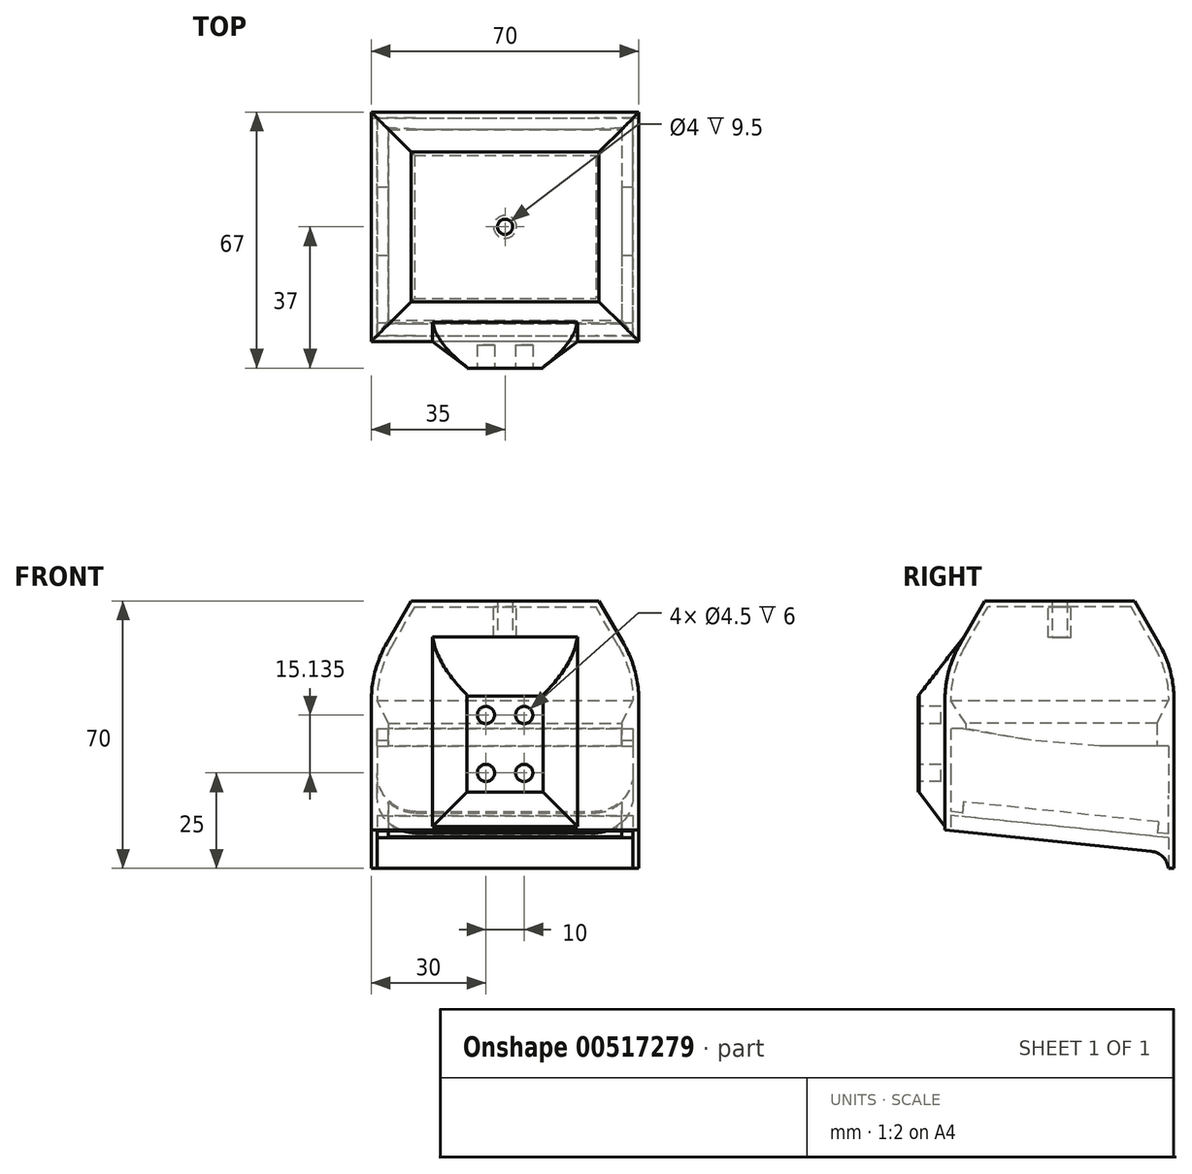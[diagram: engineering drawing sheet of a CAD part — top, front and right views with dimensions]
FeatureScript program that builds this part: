
annotation { "Feature Type Name" : "Feature", "Feature Type Description" : "" }
export const myFeature = defineFeature(function(context is Context, id is Id, definition is map)
    precondition{}
    {
        {
            var Q0;
            Q0=qCreatedBy(makeId("Top.planeOp"),FACE);
            var sketch = newSketch(context, id + "F0", { "sketchPlane" : qUnion([Q0])});
            skLineSegment(sketch, "E0.bottom", {"start": v(-35, 30) * mm, "end": v(35, 30) * mm});
            skLineSegment(sketch, "E0.top", {"start": v(-35, -30) * mm, "end": v(35, -30) * mm});
            skLineSegment(sketch, "E0.left", {"start": v(-35, 30) * mm, "end": v(-35, -30) * mm});
            skLineSegment(sketch, "E0.right", {"start": v(35, 30) * mm, "end": v(35, -30) * mm});
            skSolve(sketch);
        }
        {
            var Q0;
            Q0 = qSketchRegion(id + "F0", true);
            extrude(context, id + "F1", {"entities" : qUnion([Q0]), "endBound" : BoundingType.SYMMETRIC, "depth" : 70 * mm, "offsetDistance" : 25 * mm});
        }
        {
            var Q0;
            Q0=makeQuery(id+"F1.opExtrude","CAP_FACE",FACE,{"disambiguationData":[OSD([sQuery(id+"F0.wireOp",EDGE,"E0.bottom"),sQuery(id+"F0.wireOp",EDGE,"E0.top"),sQuery(id+"F0.wireOp",EDGE,"E0.left"),sQuery(id+"F0.wireOp",EDGE,"E0.right")])],"isStart":false});
            chamfer(context, id + "F2", {"entities" : qUnion([Q0]), "chamferType" : ChamferType.OFFSET_ANGLE, "width" : 18 * mm, "oppositeDirection" : false, "angle" : 30 * degree, "tangentPropagation" : true});
        }
        {
            var Q0;
            {var subQ0=sQuery(id+"F0.wireOp",EDGE,"E0.bottom");Q0=makeQuery(id+"F2.opChamfer","BLEND_EDGE",EDGE,{"blendedFrom":[makeQuery(id+"F1.opExtrude","CAP_EDGE",EDGE,{"disambiguationData":[OSD([subQ0])],"isStart":false}),makeQuery(id+"F1.opExtrude","SWEPT_FACE",FACE,{"disambiguationData":[OSD([subQ0])]})],"blendedInto":[makeQuery(id+"F1.opExtrude","SWEPT_FACE",FACE,{"disambiguationData":[OSD([subQ0])]})]});}
            var Q1;
            {var subQ0=sQuery(id+"F0.wireOp",EDGE,"E0.left");Q1=makeQuery(id+"F2.opChamfer","BLEND_EDGE",EDGE,{"blendedFrom":[makeQuery(id+"F1.opExtrude","CAP_EDGE",EDGE,{"disambiguationData":[OSD([subQ0])],"isStart":false}),makeQuery(id+"F1.opExtrude","SWEPT_FACE",FACE,{"disambiguationData":[OSD([subQ0])]})],"blendedInto":[makeQuery(id+"F1.opExtrude","SWEPT_FACE",FACE,{"disambiguationData":[OSD([subQ0])]})]});}
            var Q2;
            {var subQ0=sQuery(id+"F0.wireOp",EDGE,"E0.right");Q2=makeQuery(id+"F2.opChamfer","BLEND_EDGE",EDGE,{"blendedFrom":[makeQuery(id+"F1.opExtrude","CAP_EDGE",EDGE,{"disambiguationData":[OSD([subQ0])],"isStart":false}),makeQuery(id+"F1.opExtrude","SWEPT_FACE",FACE,{"disambiguationData":[OSD([subQ0])]})],"blendedInto":[makeQuery(id+"F1.opExtrude","SWEPT_FACE",FACE,{"disambiguationData":[OSD([subQ0])]})]});}
            var Q3;
            {var subQ0=sQuery(id+"F0.wireOp",EDGE,"E0.top");Q3=makeQuery(id+"F2.opChamfer","BLEND_EDGE",EDGE,{"blendedFrom":[makeQuery(id+"F1.opExtrude","CAP_EDGE",EDGE,{"disambiguationData":[OSD([subQ0])],"isStart":false}),makeQuery(id+"F1.opExtrude","SWEPT_FACE",FACE,{"disambiguationData":[OSD([subQ0])]})],"blendedInto":[makeQuery(id+"F1.opExtrude","SWEPT_FACE",FACE,{"disambiguationData":[OSD([subQ0])]})]});}
            fillet(context, id + "F3", {"entities" : qUnion([Q0, Q1, Q2, Q3]), "radius" : 30 * mm, "tangentPropagation" : true, "allowEdgeOverflow" : false});
        }
        {
            var Q0;
            Q0=makeQuery(id+"F1.opExtrude","CAP_FACE",FACE,{"disambiguationData":[OSD([sQuery(id+"F0.wireOp",EDGE,"E0.bottom"),sQuery(id+"F0.wireOp",EDGE,"E0.top"),sQuery(id+"F0.wireOp",EDGE,"E0.left"),sQuery(id+"F0.wireOp",EDGE,"E0.right")])],"isStart":true});
            var Q1;
            Q1=makeQuery(id+"F1.opExtrude","SWEPT_BODY",BODY,{"disambiguationData":[OSD([sQuery(id+"F0.wireOp",EDGE,"E0.bottom"),sQuery(id+"F0.wireOp",EDGE,"E0.top"),sQuery(id+"F0.wireOp",EDGE,"E0.left"),sQuery(id+"F0.wireOp",EDGE,"E0.right")])]});
            shell(context, id + "F4", {"entities" : qUnion([Q0]), "parts" : qUnion([Q1]), "thickness" : 1.5 * mm});
        }
        {
            var Q0;
            Q0=makeQuery(id+"F1.opExtrude","SWEPT_FACE",FACE,{"disambiguationData":[OSD([sQuery(id+"F0.wireOp",EDGE,"E0.top")])]});
            var sketch = newSketch(context, id + "F5", { "sketchPlane" : qUnion([Q0])});
            skLineSegment(sketch, "E1.bottom", {"start": v(-10, 10) * mm, "end": v(10, 10) * mm});
            skLineSegment(sketch, "E1.top", {"start": v(-10, -15) * mm, "end": v(10, -15) * mm});
            skLineSegment(sketch, "E1.left", {"start": v(-10, 10) * mm, "end": v(-10, -15) * mm});
            skLineSegment(sketch, "E1.right", {"start": v(10, 10) * mm, "end": v(10, -15) * mm});
            skSolve(sketch);
        }
        {
            var Q0;
            Q0 = qSketchRegion(id + "F5", true);
            extrude(context, id + "F6", {"entities" : qUnion([Q0]), "operationType" : NewBodyOperationType.ADD, "depth" : 7 * mm, "offsetDistance" : 25 * mm, "hasSecondDirection" : true, "secondDirectionOppositeDirection" : true, "secondDirectionDepth" : 1.5 * mm});
        }
        {
            var Q0;
            Q0=makeQuery(id+"F6.boolean.opBoolean","INTERSECT",EDGE,{"derivedFrom":[makeQuery(id+"F3.opFillet","BLEND_FACE",FACE,{"disambiguationData":[OSD([sQuery(id+"F0.wireOp",EDGE,"E0.top")])]}),makeQuery(id+"F6.opExtrude","SWEPT_FACE",FACE,{"disambiguationData":[OSD([sQuery(id+"F5.wireOp",EDGE,"E1.bottom")])]})]});
            chamfer(context, id + "F7", {"entities" : qUnion([Q0]), "chamferType" : ChamferType.OFFSET_ANGLE, "width" : 15 * mm, "oppositeDirection" : false, "angle" : 58 * degree, "tangentPropagation" : true});
        }
        {
            var Q0;
            Q0=makeQuery(id+"F6.boolean.opBoolean","INTERSECT",EDGE,{"derivedFrom":[makeQuery(id+"F1.opExtrude","SWEPT_FACE",FACE,{"disambiguationData":[OSD([sQuery(id+"F0.wireOp",EDGE,"E0.top")])]}),makeQuery(id+"F6.opExtrude","SWEPT_FACE",FACE,{"disambiguationData":[OSD([sQuery(id+"F5.wireOp",EDGE,"E1.right")])]})]});
            var Q1;
            Q1=makeQuery(id+"F6.boolean.opBoolean","INTERSECT",EDGE,{"derivedFrom":[makeQuery(id+"F1.opExtrude","SWEPT_FACE",FACE,{"disambiguationData":[OSD([sQuery(id+"F0.wireOp",EDGE,"E0.top")])]}),makeQuery(id+"F6.opExtrude","SWEPT_FACE",FACE,{"disambiguationData":[OSD([sQuery(id+"F5.wireOp",EDGE,"E1.top")])]})]});
            var Q2;
            Q2=makeQuery(id+"F6.boolean.opBoolean","INTERSECT",EDGE,{"derivedFrom":[makeQuery(id+"F1.opExtrude","SWEPT_FACE",FACE,{"disambiguationData":[OSD([sQuery(id+"F0.wireOp",EDGE,"E0.top")])]}),makeQuery(id+"F6.opExtrude","SWEPT_FACE",FACE,{"disambiguationData":[OSD([sQuery(id+"F5.wireOp",EDGE,"E1.left")])]})]});
            chamfer(context, id + "F8", {"entities" : qUnion([Q0, Q1, Q2]), "chamferType" : ChamferType.OFFSET_ANGLE, "width" : 9 * mm, "oppositeDirection" : false, "angle" : 37 * degree, "tangentPropagation" : true});
        }
        {
            var Q0;
            Q0=makeQuery(id+"F6.opExtrude","CAP_FACE",FACE,{"disambiguationData":[OSD([sQuery(id+"F5.wireOp",EDGE,"E1.bottom"),sQuery(id+"F5.wireOp",EDGE,"E1.top"),sQuery(id+"F5.wireOp",EDGE,"E1.left"),sQuery(id+"F5.wireOp",EDGE,"E1.right")])],"isStart":false});
            var sketch = newSketch(context, id + "F9", { "sketchPlane" : qUnion([Q0])});
            skLineSegment(sketch, "E2.0", {"start": v(5, -10) * mm, "end": v(5, 5.14) * mm, "construction": true});
            skLineSegment(sketch, "E2.1", {"start": v(-5, -10) * mm, "end": v(5, -10) * mm, "construction": true});
            skLineSegment(sketch, "E2.2", {"start": v(-5, 5.14) * mm, "end": v(-5, -10) * mm, "construction": true});
            skLineSegment(sketch, "E2.3", {"start": v(5, 5.14) * mm, "end": v(-5, 5.14) * mm, "construction": true});
            skCircle(sketch, "E3", {"center": v(-5, 5.14) * mm, "radius": 2.25 * mm});
            skCircle(sketch, "E4.MirrorC", {"center": v(5, 5.14) * mm, "radius": 2.25 * mm});
            skCircle(sketch, "E5", {"center": v(-5, -10) * mm, "radius": 2.25 * mm});
            skCircle(sketch, "E6.MirrorC", {"center": v(5, -10) * mm, "radius": 2.25 * mm});
            skSolve(sketch);
        }
        {
            var Q0;
            Q0 = qSketchRegion(id + "F9", true);
            extrude(context, id + "F10", {"entities" : qUnion([Q0]), "operationType" : NewBodyOperationType.REMOVE, "oppositeDirection" : true, "depth" : 6 * mm, "offsetDistance" : 25 * mm});
        }
        {
            var Q0;
            Q0=makeQuery(id+"F1.opExtrude","SWEPT_FACE",FACE,{"disambiguationData":[OSD([sQuery(id+"F0.wireOp",EDGE,"E0.left")])]});
            var sketch = newSketch(context, id + "F11", { "sketchPlane" : qUnion([Q0])});
            skLineSegment(sketch, "E7", {"start": v(-28.5, -35) * mm, "end": v(30, -35) * mm});
            skLineSegment(sketch, "E8", {"start": v(30, -35) * mm, "end": v(30, -25) * mm});
            skLineSegment(sketch, "E9", {"start": v(30, -25) * mm, "end": v(-28.5, -31) * mm});
            skLineSegment(sketch, "E10", {"start": v(-28.5, -31) * mm, "end": v(-28.5, -35) * mm});
            skSolve(sketch);
        }
        {
            var Q0;
            Q0 = qSketchRegion(id + "F11", true);
            extrude(context, id + "F12", {"entities" : qUnion([Q0]), "operationType" : NewBodyOperationType.REMOVE, "endBound" : BoundingType.THROUGH_ALL, "oppositeDirection" : true, "depth" : 25 * mm, "offsetDistance" : 25 * mm});
        }
        {
            var Q0;
            {var subQ0=sQuery(id+"F11.wireOp",EDGE,"E9");var subQ2=sQuery(id+"F0.wireOp",EDGE,"E0.left");var subQ3=makeQuery(id+"F1.opExtrude","SWEPT_FACE",FACE,{"disambiguationData":[OSD([subQ2])]});var subQ4=sQuery(id+"F11.wireOp",EDGE,"E10");Q0=makeQuery(id+"F12.boolean.opBoolean","COPY",EDGE,{"disambiguationData":[TD([subQ3])],"derivedFrom":makeQuery(id+"F12.opExtrude","SWEPT_EDGE",EDGE,{"disambiguationData":[OSD([subQ0,subQ4])]})});}
            var Q1;
            {var subQ1=sQuery(id+"F11.wireOp",EDGE,"E9");var subQ2=sQuery(id+"F0.wireOp",EDGE,"E0.right");var subQ3=makeQuery(id+"F1.opExtrude","SWEPT_FACE",FACE,{"disambiguationData":[OSD([subQ2])]});var subQ4=sQuery(id+"F11.wireOp",EDGE,"E10");Q1=makeQuery(id+"F12.boolean.opBoolean","COPY",EDGE,{"disambiguationData":[TD([subQ3])],"derivedFrom":makeQuery(id+"F12.opExtrude","SWEPT_EDGE",EDGE,{"disambiguationData":[OSD([subQ1,subQ4])]})});}
            fillet(context, id + "F13", {"entities" : qUnion([Q0, Q1]), "radius" : 5 * mm, "tangentPropagation" : true, "allowEdgeOverflow" : false});
        }
        {
            var Q0;
            {var subQ0=sQuery(id+"F0.wireOp",EDGE,"E0.top");Q0=makeQuery(id+"F4.opShell","OFFSET_FACE",FACE,{"disambiguationData":[OSD([subQ0]),TDD([makeQuery(id+"F1.opExtrude","SWEPT_FACE",FACE,{"disambiguationData":[OSD([subQ0])]})])]});}
            var sketch = newSketch(context, id + "F14", { "sketchPlane" : qUnion([Q0])});
            skLineSegment(sketch, "E11", {"start": v(-33.5, 8.96) * mm, "end": v(-33.5, 2.96) * mm});
            skLineSegment(sketch, "E12", {"start": v(-33.5, 2.96) * mm, "end": v(-30.5, 2.96) * mm});
            skLineSegment(sketch, "E13", {"start": v(-30.5, 2.96) * mm, "end": v(-33.5, 8.96) * mm});
            skLineSegment(sketch, "E14", {"start": v(33.5, 8.96) * mm, "end": v(33.5, 2.96) * mm});
            skLineSegment(sketch, "E15", {"start": v(33.5, 2.96) * mm, "end": v(30.5, 2.96) * mm});
            skLineSegment(sketch, "E16", {"start": v(30.5, 2.96) * mm, "end": v(33.5, 8.96) * mm});
            skSolve(sketch);
        }
        {
            var Q0;
            Q0 = qSketchRegion(id + "F14", true);
            extrude(context, id + "F15", {"entities" : qUnion([Q0]), "operationType" : NewBodyOperationType.ADD, "endBound" : BoundingType.UP_TO_NEXT, "depth" : 0 * mm, "offsetDistance" : 25 * mm});
        }
        {
            var Q0;
            {var subQ1=sQuery(id+"F0.wireOp",EDGE,"E0.right");Q0=makeQuery(id+"F18.boolean.opBoolean","SPLIT",FACE,{"disambiguationData":[TD([makeQuery(id+"F18.opExtrude","SWEPT_FACE",FACE,{"disambiguationData":[OSD([sQuery(id+"F17.wireOp",EDGE,"E25")])]})])],"derivedFrom":makeQuery(id+"F4.opShell","OFFSET_FACE",FACE,{"disambiguationData":[OSD([subQ1]),TDD([makeQuery(id+"F1.opExtrude","SWEPT_FACE",FACE,{"disambiguationData":[OSD([subQ1])]})])]})});}
            var sketch = newSketch(context, id + "F16", { "sketchPlane" : qUnion([Q0])});
            skLineSegment(sketch, "E17", {"start": v(28.5, 8.96) * mm, "end": v(28.5, 2.96) * mm});
            skLineSegment(sketch, "E18", {"start": v(28.5, 2.96) * mm, "end": v(24.5, 2.96) * mm});
            skLineSegment(sketch, "E19", {"start": v(24.5, 2.96) * mm, "end": v(28.5, 8.96) * mm});
            skLineSegment(sketch, "E20", {"start": v(-28.5, 8.96) * mm, "end": v(-28.5, 2.96) * mm});
            skLineSegment(sketch, "E21", {"start": v(-28.5, 2.96) * mm, "end": v(-25.5, 2.96) * mm});
            skLineSegment(sketch, "E22", {"start": v(-25.5, 2.96) * mm, "end": v(-28.5, 8.96) * mm});
            skSolve(sketch);
        }
        {
            var Q0;
            {var subQ0=sQuery(id+"F0.wireOp",EDGE,"E0.right");Q0=makeQuery(id+"F4.opShell","OFFSET_FACE",FACE,{"disambiguationData":[OSD([subQ0]),TDD([makeQuery(id+"F1.opExtrude","SWEPT_FACE",FACE,{"disambiguationData":[OSD([subQ0])]})])]});}
            var sketch = newSketch(context, id + "F17", { "sketchPlane" : qUnion([Q0])});
            skLineSegment(sketch, "E23", {"start": v(-28.5, -26.98) * mm, "end": v(28.5, -21.13) * mm});
            skLineSegment(sketch, "E24", {"start": v(28.5, -21.13) * mm, "end": v(28.5, -20.13) * mm});
            skLineSegment(sketch, "E25", {"start": v(28.5, -20.13) * mm, "end": v(-28.5, -25.98) * mm});
            skLineSegment(sketch, "E26", {"start": v(-28.5, -25.98) * mm, "end": v(-28.5, -26.98) * mm});
            skSolve(sketch);
        }
        {
            var Q0;
            Q0 = qSketchRegion(id + "F17", true);
            extrude(context, id + "F18", {"entities" : qUnion([Q0]), "operationType" : NewBodyOperationType.ADD, "endBound" : BoundingType.UP_TO_NEXT, "depth" : 25 * mm, "offsetDistance" : 25 * mm});
        }
        {
            var Q0;
            Q0=makeQuery(id+"F18.opExtrude","SWEPT_FACE",FACE,{"disambiguationData":[OSD([sQuery(id+"F17.wireOp",EDGE,"E23")])]});
            var sketch = newSketch(context, id + "F19", { "sketchPlane" : qUnion([Q0])});
            skLineSegment(sketch, "E27.0", {"start": v(30.5, 23.2) * mm, "end": v(-30.5, 23.2) * mm});
            skLineSegment(sketch, "E27.1", {"start": v(30.5, -28.1) * mm, "end": v(30.5, 23.2) * mm});
            skLineSegment(sketch, "E27.2", {"start": v(-30.5, -28.1) * mm, "end": v(30.5, -28.1) * mm});
            skLineSegment(sketch, "E27.3", {"start": v(-30.5, 23.2) * mm, "end": v(-30.5, -28.1) * mm});
            skSolve(sketch);
        }
        {
            var Q0;
            Q0 = qSketchRegion(id + "F19", true);
            extrude(context, id + "F20", {"entities" : qUnion([Q0]), "operationType" : NewBodyOperationType.REMOVE, "oppositeDirection" : true, "depth" : 1 * mm, "offsetDistance" : 25 * mm});
        }
        {
            var Q0;
            Q0=makeQuery(id+"F18.opExtrude","SWEPT_EDGE",EDGE,{"disambiguationData":[OSD([sQuery(id+"F0.wireOp",EDGE,"E0.top"),sQuery(id+"F0.wireOp",EDGE,"E0.right"),sQuery(id+"F17.wireOp",EDGE,"E24"),sQuery(id+"F17.wireOp",EDGE,"E25")])]});
            var Q1;
            Q1=makeQuery(id+"F18.opExtrude","CAP_EDGE",EDGE,{"disambiguationData":[OSD([sQuery(id+"F17.wireOp",EDGE,"E25")])],"isStart":true});
            var Q2;
            Q2=makeQuery(id+"F18.opExtrude","SWEPT_EDGE",EDGE,{"disambiguationData":[OSD([sQuery(id+"F0.wireOp",EDGE,"E0.bottom"),sQuery(id+"F0.wireOp",EDGE,"E0.right"),sQuery(id+"F17.wireOp",EDGE,"E25"),sQuery(id+"F17.wireOp",EDGE,"E26")])]});
            var Q3;
            Q3=makeQuery(id+"F18.opExtrude","CAP_EDGE",EDGE,{"disambiguationData":[OSD([sQuery(id+"F17.wireOp",EDGE,"E25")])],"isStart":false});
            fillet(context, id + "F21", {"entities" : qUnion([Q0, Q1, Q2, Q3]), "radius" : 10 * mm, "tangentPropagation" : true, "allowEdgeOverflow" : false});
        }
        {
            var Q0;
            Q0 = qSketchRegion(id + "F16", true);
            extrude(context, id + "F22", {"entities" : qUnion([Q0]), "operationType" : NewBodyOperationType.ADD, "depth" : 68 * mm, "offsetDistance" : 25 * mm});
        }
        {
            var Q0;
            {var subQ2=sQuery(id+"F0.wireOp",EDGE,"E0.right");Q0=makeQuery(id+"F18.boolean.opBoolean","SPLIT",FACE,{"disambiguationData":[TD([makeQuery(id+"F15.opExtrude","SWEPT_FACE",FACE,{"disambiguationData":[OSD([sQuery(id+"F14.wireOp",EDGE,"E12")])]})])],"derivedFrom":makeQuery(id+"F4.opShell","OFFSET_FACE",FACE,{"disambiguationData":[OSD([subQ2]),TDD([makeQuery(id+"F1.opExtrude","SWEPT_FACE",FACE,{"disambiguationData":[OSD([subQ2])]})])]})});}
            var sketch = newSketch(context, id + "F23", { "sketchPlane" : qUnion([Q0])});
            skLineSegment(sketch, "E28", {"start": v(28.5, 2.96) * mm, "end": v(28.5, 1.66) * mm});
            skLineSegment(sketch, "E29", {"start": v(28.5, 1.66) * mm, "end": v(25.16, 1.66) * mm});
            skLineSegment(sketch, "E30", {"start": v(25.16, 1.66) * mm, "end": v(7.43, -1.47) * mm});
            skLineSegment(sketch, "E31", {"start": v(7.43, -1.47) * mm, "end": v(-10.5, -3.04) * mm});
            skLineSegment(sketch, "E32", {"start": v(-10.5, -3.04) * mm, "end": v(-28.5, -3.04) * mm});
            skLineSegment(sketch, "E33", {"start": v(-28.5, -3.04) * mm, "end": v(-28.5, 2.96) * mm});
            skLineSegment(sketch, "E34", {"start": v(-28.5, 2.96) * mm, "end": v(28.5, 2.96) * mm});
            skSolve(sketch);
        }
        {
            var Q0;
            Q0 = qSketchRegion(id + "F23", true);
            extrude(context, id + "F24", {"entities" : qUnion([Q0]), "operationType" : NewBodyOperationType.ADD, "endBound" : BoundingType.UP_TO_NEXT, "depth" : 25 * mm, "offsetDistance" : 25 * mm});
        }
        {
            var Q0;
            Q0=makeQuery(id+"F24.opExtrude","SWEPT_FACE",FACE,{"disambiguationData":[OSD([sQuery(id+"F23.wireOp",EDGE,"E32")])]});
            var sketch = newSketch(context, id + "F25", { "sketchPlane" : qUnion([Q0])});
            skLineSegment(sketch, "E35.bottom", {"start": v(30.5, -25.5) * mm, "end": v(-30.5, -25.5) * mm});
            skLineSegment(sketch, "E35.top", {"start": v(30.5, 24.5) * mm, "end": v(-30.5, 24.5) * mm});
            skLineSegment(sketch, "E35.left", {"start": v(30.5, -25.5) * mm, "end": v(30.5, 24.5) * mm});
            skLineSegment(sketch, "E35.right", {"start": v(-30.5, -25.5) * mm, "end": v(-30.5, 24.5) * mm});
            skSolve(sketch);
        }
        {
            var Q0;
            Q0 = qSketchRegion(id + "F25", true);
            extrude(context, id + "F26", {"entities" : qUnion([Q0]), "operationType" : NewBodyOperationType.REMOVE, "oppositeDirection" : true, "depth" : 10 * mm, "offsetDistance" : 25 * mm});
        }
        {
            var Q0;
            Q0=makeQuery(id+"F4.opShell","OFFSET_FACE",FACE,{"disambiguationData":[OSD([sQuery(id+"F0.wireOp",EDGE,"E0.bottom"),sQuery(id+"F0.wireOp",EDGE,"E0.top"),sQuery(id+"F0.wireOp",EDGE,"E0.left"),sQuery(id+"F0.wireOp",EDGE,"E0.right")])]});
            var sketch = newSketch(context, id + "F27", { "sketchPlane" : qUnion([Q0])});
            skCircle(sketch, "E36", {"center": v(0, 0) * mm, "radius": 3 * mm});
            skSolve(sketch);
        }
        {
            var Q0;
            Q0 = qSketchRegion(id + "F27", true);
            extrude(context, id + "F28", {"entities" : qUnion([Q0]), "operationType" : NewBodyOperationType.ADD, "depth" : 8 * mm, "offsetDistance" : 25 * mm});
        }
        {
            var Q0;
            Q0=makeQuery(id+"F28.opExtrude","CAP_FACE",FACE,{"disambiguationData":[OSD([sQuery(id+"F27.wireOp",EDGE,"E36")])],"isStart":false});
            var sketch = newSketch(context, id + "F29", { "sketchPlane" : qUnion([Q0])});
            skCircle(sketch, "E37", {"center": v(0, 0) * mm, "radius": 2 * mm});
            skSolve(sketch);
        }
        {
            var Q0;
            Q0 = qSketchRegion(id + "F29", true);
            extrude(context, id + "F30", {"entities" : qUnion([Q0]), "operationType" : NewBodyOperationType.REMOVE, "endBound" : BoundingType.THROUGH_ALL, "oppositeDirection" : true, "depth" : 25 * mm, "offsetDistance" : 25 * mm});
        }
    });
